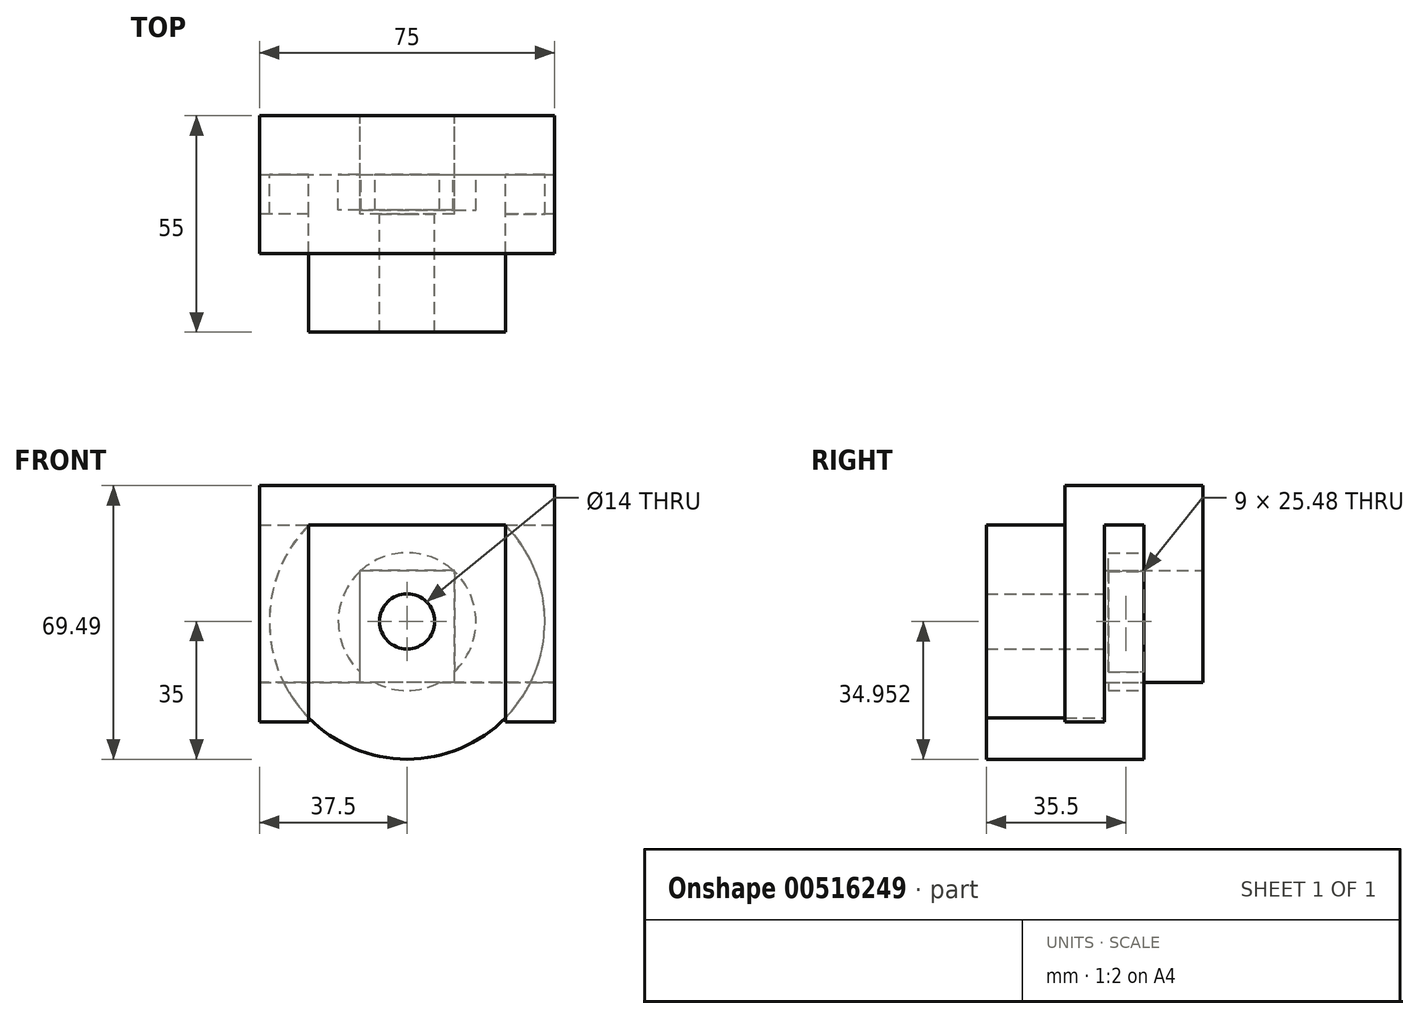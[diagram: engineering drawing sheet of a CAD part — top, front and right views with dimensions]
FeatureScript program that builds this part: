
annotation { "Feature Type Name" : "Feature", "Feature Type Description" : "" }
export const myFeature = defineFeature(function(context is Context, id is Id, definition is map)
    precondition{}
    {
        {
            var Q0;
            Q0=qCreatedBy(makeId("Front.planeOp"),FACE);
            var sketch = newSketch(context, id + "F0", { "sketchPlane" : qUnion([Q0])});
            skCircle(sketch, "E0", {"center": v(0, 0) * mm, "radius": 35 * mm});
            skCircle(sketch, "E1", {"center": v(0, 0) * mm, "radius": 7 * mm});
            skSolve(sketch);
        }
        {
            var Q0;
            Q0 = qSketchRegion(id + "F0UFtEnd2K3w3mr_0", true);
            var Q1;
            Q1=makeQuery(id+"F0.imprint","IMPRINT",FACE,{"disambiguationData":[TD([[makeQuery(id+"F0.imprint","IMPRINT",EDGE,{"derivedFrom":sQuery(id+"F0.wireOp",EDGE,"E0")}),1.0]])]});
            extrude(context, id + "F1", {"entities" : qUnion([Q0, Q1]), "endBound" : BoundingType.SYMMETRIC, "depth" : 40 * mm, "offsetDistance" : 25 * mm});
        }
        {
            var Q0;
            Q0=qCreatedBy(makeId("Top.planeOp"),FACE);
            var sketch = newSketch(context, id + "F2", { "sketchPlane" : qUnion([Q0])});
            skLineSegment(sketch, "E2", {"start": v(35, 30.24) * mm, "end": v(35, -20) * mm});
            skLineSegment(sketch, "E3", {"start": v(-35, -20) * mm, "end": v(-35, 20) * mm});
            skLineSegment(sketch, "E4.bottom", {"start": v(-35, -20) * mm, "end": v(-25, -20) * mm});
            skLineSegment(sketch, "E4.top", {"start": v(-35, 10) * mm, "end": v(-25, 10) * mm});
            skLineSegment(sketch, "E4.left", {"start": v(-35, -20) * mm, "end": v(-35, 10) * mm});
            skLineSegment(sketch, "E4.right", {"start": v(-25, -20) * mm, "end": v(-25, 10) * mm});
            skLineSegment(sketch, "E5.bottom", {"start": v(35, -20) * mm, "end": v(25, -20) * mm});
            skLineSegment(sketch, "E5.top", {"start": v(35, 10) * mm, "end": v(25, 10) * mm});
            skLineSegment(sketch, "E5.left", {"start": v(35, -20) * mm, "end": v(35, 10) * mm});
            skLineSegment(sketch, "E5.right", {"start": v(25, -20) * mm, "end": v(25, 10) * mm});
            skSolve(sketch);
        }
        {
            var Q0;
            Q0=makeQuery(id+"F2.imprint","IMPRINT",FACE,{"disambiguationData":[TD([[makeQuery(id+"F2.imprint","IMPRINT",EDGE,{"derivedFrom":sQuery(id+"F2.wireOp",EDGE,"E5.bottom")}),-1.0]])]});
            var Q1;
            Q1=makeQuery(id+"F2.imprint","IMPRINT",FACE,{"disambiguationData":[TD([[makeQuery(id+"F2.imprint","IMPRINT",EDGE,{"derivedFrom":sQuery(id+"F2.wireOp",EDGE,"E4.bottom")}),1.0]])]});
            extrude(context, id + "F3", {"entities" : qUnion([Q0, Q1]), "operationType" : NewBodyOperationType.REMOVE, "endBound" : BoundingType.SYMMETRIC, "depth" : 70 * mm, "offsetDistance" : 25 * mm});
        }
        {
            var Q0;
            Q0=makeQuery(id+"F3.boolean.opBoolean","COPY",FACE,{"derivedFrom":makeQuery(id+"F3.opExtrude","SWEPT_FACE",FACE,{"disambiguationData":[OSD([sQuery(id+"F2.wireOp",EDGE,"E5.right")])]})});
            var sketch = newSketch(context, id + "F4", { "sketchPlane" : qUnion([Q0])});
            skLineSegment(sketch, "E6.bottom", {"start": v(-20, 24.5) * mm, "end": v(20, 24.5) * mm});
            skLineSegment(sketch, "E6.top", {"start": v(-20, 35) * mm, "end": v(20, 35) * mm});
            skLineSegment(sketch, "E6.left", {"start": v(-20, 24.5) * mm, "end": v(-20, 35) * mm});
            skLineSegment(sketch, "E6.right", {"start": v(20, 24.5) * mm, "end": v(20, 35) * mm});
            skLineSegment(sketch, "E7", {"start": v(20, -35) * mm, "end": v(-20, -35) * mm});
            skSolve(sketch);
        }
        {
            var Q0;
            Q0=makeQuery(id+"F4.imprint","IMPRINT",FACE,{"disambiguationData":[TD([[makeQuery(id+"F4.imprint","IMPRINT",EDGE,{"derivedFrom":sQuery(id+"F4.wireOp",EDGE,"E6.bottom")}),1.0]])]});
            extrude(context, id + "F5", {"entities" : qUnion([Q0]), "operationType" : NewBodyOperationType.REMOVE, "oppositeDirection" : true, "depth" : 70 * mm, "offsetDistance" : 25 * mm});
        }
        {
            var Q0;
            Q0=makeQuery(id+"F1.opExtrude","CAP_FACE",FACE,{"disambiguationData":[OSD([sQuery(id+"F0.wireOp",EDGE,"E0"),sQuery(id+"F0.wireOp",EDGE,"E1")])],"isStart":true});
            var sketch = newSketch(context, id + "F6", { "sketchPlane" : qUnion([Q0])});
            skCircle(sketch, "E8", {"center": v(0, -0.05) * mm, "radius": 17.5 * mm});
            skSolve(sketch);
        }
        {
            var Q0;
            Q0=makeQuery(id+"F6.imprint","IMPRINT",FACE,{"disambiguationData":[TD([[makeQuery(id+"F6.imprint","IMPRINT",EDGE,{"derivedFrom":sQuery(id+"F6.wireOp",EDGE,"E8")}),1.0]])]});
            extrude(context, id + "F7", {"entities" : qUnion([Q0]), "operationType" : NewBodyOperationType.REMOVE, "oppositeDirection" : true, "depth" : 9 * mm, "offsetDistance" : 25 * mm});
        }
        {
            var Q0;
            Q0=makeQuery(id+"F3.boolean.opBoolean","COPY",FACE,{"derivedFrom":makeQuery(id+"F3.opExtrude","SWEPT_FACE",FACE,{"disambiguationData":[OSD([sQuery(id+"F2.wireOp",EDGE,"E5.top")])]})});
            var sketch = newSketch(context, id + "F8", { "sketchPlane" : qUnion([Q0])});
            skLineSegment(sketch, "E9", {"start": v(-37.5, -25.5) * mm, "end": v(-37.5, 34.5) * mm});
            skLineSegment(sketch, "E10", {"start": v(-37.5, 34.5) * mm, "end": v(37.5, 34.5) * mm});
            skLineSegment(sketch, "E11", {"start": v(37.5, 34.5) * mm, "end": v(37.5, -25.5) * mm});
            skLineSegment(sketch, "E12", {"start": v(37.5, -25.5) * mm, "end": v(25, -25.5) * mm});
            skLineSegment(sketch, "E13", {"start": v(25, -25.5) * mm, "end": v(25, 24.5) * mm});
            skLineSegment(sketch, "E14", {"start": v(25, 24.5) * mm, "end": v(-25, 24.5) * mm});
            skLineSegment(sketch, "E15", {"start": v(-25, 24.5) * mm, "end": v(-25, -25.5) * mm});
            skLineSegment(sketch, "E16", {"start": v(-25, -25.5) * mm, "end": v(-37.5, -25.5) * mm});
            skSolve(sketch);
        }
        {
            var Q0;
            Q0 = qSketchRegion(id + "FKbgH9zVBHbA3CD_1", true);
            var Q1;
            {var subQ1=makeQuery(id+"F3.boolean.opBoolean","INTERSECT",EDGE,{"derivedFrom":[makeQuery(id+"F1.opExtrude","SWEPT_FACE",FACE,{"disambiguationData":[OSD([sQuery(id+"F0.wireOp",EDGE,"E0")])]}),makeQuery(id+"F3.opExtrude","SWEPT_FACE",FACE,{"disambiguationData":[OSD([sQuery(id+"F2.wireOp",EDGE,"E5.top")])]})]});Q1=makeQuery(id+"F8.imprint","IMPRINT",FACE,{"disambiguationData":[TD([[makeQuery(id+"F8.imprint","IMPRINT",EDGE,{"derivedFrom":subQ1}),1.0]])]});}
            var Q2;
            Q2=makeQuery(id+"F8.imprint","IMPRINT",FACE,{"disambiguationData":[TD([[makeQuery(id+"F8.imprint","IMPRINT",EDGE,{"derivedFrom":sQuery(id+"F8.wireOp",EDGE,"E9")}),-1.0]])]});
            extrude(context, id + "F9", {"entities" : qUnion([Q0, Q1, Q2]), "depth" : 10 * mm, "offsetDistance" : 25 * mm});
        }
        {
            var Q0;
            Q0=makeQuery(id+"F9.opExtrude","CAP_FACE",FACE,{"disambiguationData":[OSD([sQuery(id+"F8.wireOp",EDGE,"E9"),sQuery(id+"F8.wireOp",EDGE,"E10"),sQuery(id+"F8.wireOp",EDGE,"E11"),sQuery(id+"F8.wireOp",EDGE,"E12"),sQuery(id+"F8.wireOp",EDGE,"E13"),sQuery(id+"F8.wireOp",EDGE,"E14"),sQuery(id+"F8.wireOp",EDGE,"E15"),sQuery(id+"F8.wireOp",EDGE,"E16")])],"isStart":true});
            var sketch = newSketch(context, id + "F10", { "sketchPlane" : qUnion([Q0])});
            skLineSegment(sketch, "E17.bottom", {"start": v(-37.5, 34.5) * mm, "end": v(37.5, 34.5) * mm});
            skLineSegment(sketch, "E17.top", {"start": v(-37.5, 24.5) * mm, "end": v(37.5, 24.5) * mm});
            skLineSegment(sketch, "E17.left", {"start": v(-37.5, 34.5) * mm, "end": v(-37.5, 24.5) * mm});
            skLineSegment(sketch, "E17.right", {"start": v(37.5, 34.5) * mm, "end": v(37.5, 24.5) * mm});
            skSolve(sketch);
        }
        {
            var Q0;
            Q0=makeQuery(id+"F10.imprint","IMPRINT",FACE,{"disambiguationData":[TD([[makeQuery(id+"F10.imprint","IMPRINT",EDGE,{"derivedFrom":sQuery(id+"F10.wireOp",EDGE,"E17.bottom")}),1.0]])]});
            extrude(context, id + "F11", {"entities" : qUnion([Q0]), "operationType" : NewBodyOperationType.ADD, "depth" : 25 * mm, "offsetDistance" : 25 * mm});
        }
        {
            var Q0;
            Q0=makeQuery(id+"F11.boolean.opBoolean","MERGE",FACE,{"derivedFrom":[makeQuery(id+"F9.opExtrude","SWEPT_FACE",FACE,{"disambiguationData":[OSD([sQuery(id+"F8.wireOp",EDGE,"E14")])]}),makeQuery(id+"F11.opExtrude","SWEPT_FACE",FACE,{"disambiguationData":[OSD([sQuery(id+"F10.wireOp",EDGE,"E17.top")])]})]});
            var sketch = newSketch(context, id + "F12", { "sketchPlane" : qUnion([Q0])});
            skLineSegment(sketch, "E18.bottom", {"start": v(37.5, -35) * mm, "end": v(-37.5, -35) * mm});
            skLineSegment(sketch, "E18.top", {"start": v(37.5, -20) * mm, "end": v(-37.5, -20) * mm});
            skLineSegment(sketch, "E18.left", {"start": v(37.5, -35) * mm, "end": v(37.5, -20) * mm});
            skLineSegment(sketch, "E18.right", {"start": v(-37.5, -35) * mm, "end": v(-37.5, -20) * mm});
            skSolve(sketch);
        }
        {
            var Q0;
            Q0=makeQuery(id+"F12.imprint","IMPRINT",FACE,{"disambiguationData":[TD([[makeQuery(id+"F12.imprint","IMPRINT",EDGE,{"derivedFrom":sQuery(id+"F12.wireOp",EDGE,"E18.bottom")}),-1.0]])]});
            extrude(context, id + "F13", {"entities" : qUnion([Q0]), "operationType" : NewBodyOperationType.ADD, "depth" : 40 * mm, "offsetDistance" : 25 * mm});
        }
        {
            var Q0;
            Q0=makeQuery(id+"F13.boolean.opBoolean","MERGE",FACE,{"derivedFrom":[makeQuery(id+"F11.opExtrude","CAP_FACE",FACE,{"disambiguationData":[OSD([sQuery(id+"F10.wireOp",EDGE,"E17.bottom"),sQuery(id+"F10.wireOp",EDGE,"E17.top"),sQuery(id+"F10.wireOp",EDGE,"E17.left"),sQuery(id+"F10.wireOp",EDGE,"E17.right")])],"isStart":false}),makeQuery(id+"F13.opExtrude","SWEPT_FACE",FACE,{"disambiguationData":[OSD([sQuery(id+"F12.wireOp",EDGE,"E18.bottom")])]})]});
            var sketch = newSketch(context, id + "F14", { "sketchPlane" : qUnion([Q0])});
            skLineSegment(sketch, "E19.bottom", {"start": v(-12, -15.5) * mm, "end": v(12, -15.5) * mm});
            skLineSegment(sketch, "E19.top", {"start": v(-12, 13) * mm, "end": v(12, 13) * mm});
            skLineSegment(sketch, "E19.left", {"start": v(-12, -15.5) * mm, "end": v(-12, 13) * mm});
            skLineSegment(sketch, "E19.right", {"start": v(12, -15.5) * mm, "end": v(12, 13) * mm});
            skSolve(sketch);
        }
        {
            var Q0;
            Q0=makeQuery(id+"F14.imprint","IMPRINT",FACE,{"disambiguationData":[TD([[makeQuery(id+"F14.imprint","IMPRINT",EDGE,{"derivedFrom":sQuery(id+"F14.wireOp",EDGE,"E19.bottom")}),1.0]])]});
            var Q1;
            Q1=makeQuery(id+"F1.opExtrude","SWEPT_BODY",BODY,{"disambiguationData":[OSD([sQuery(id+"F0.wireOp",EDGE,"E0"),sQuery(id+"F0.wireOp",EDGE,"E1")])]});
            extrude(context, id + "F15", {"entities" : qUnion([Q0]), "operationType" : NewBodyOperationType.REMOVE, "oppositeDirection" : true, "depth" : 25 * mm, "endBoundEntityBody" : qUnion([Q1]), "offsetDistance" : 25 * mm});
        }
    });
